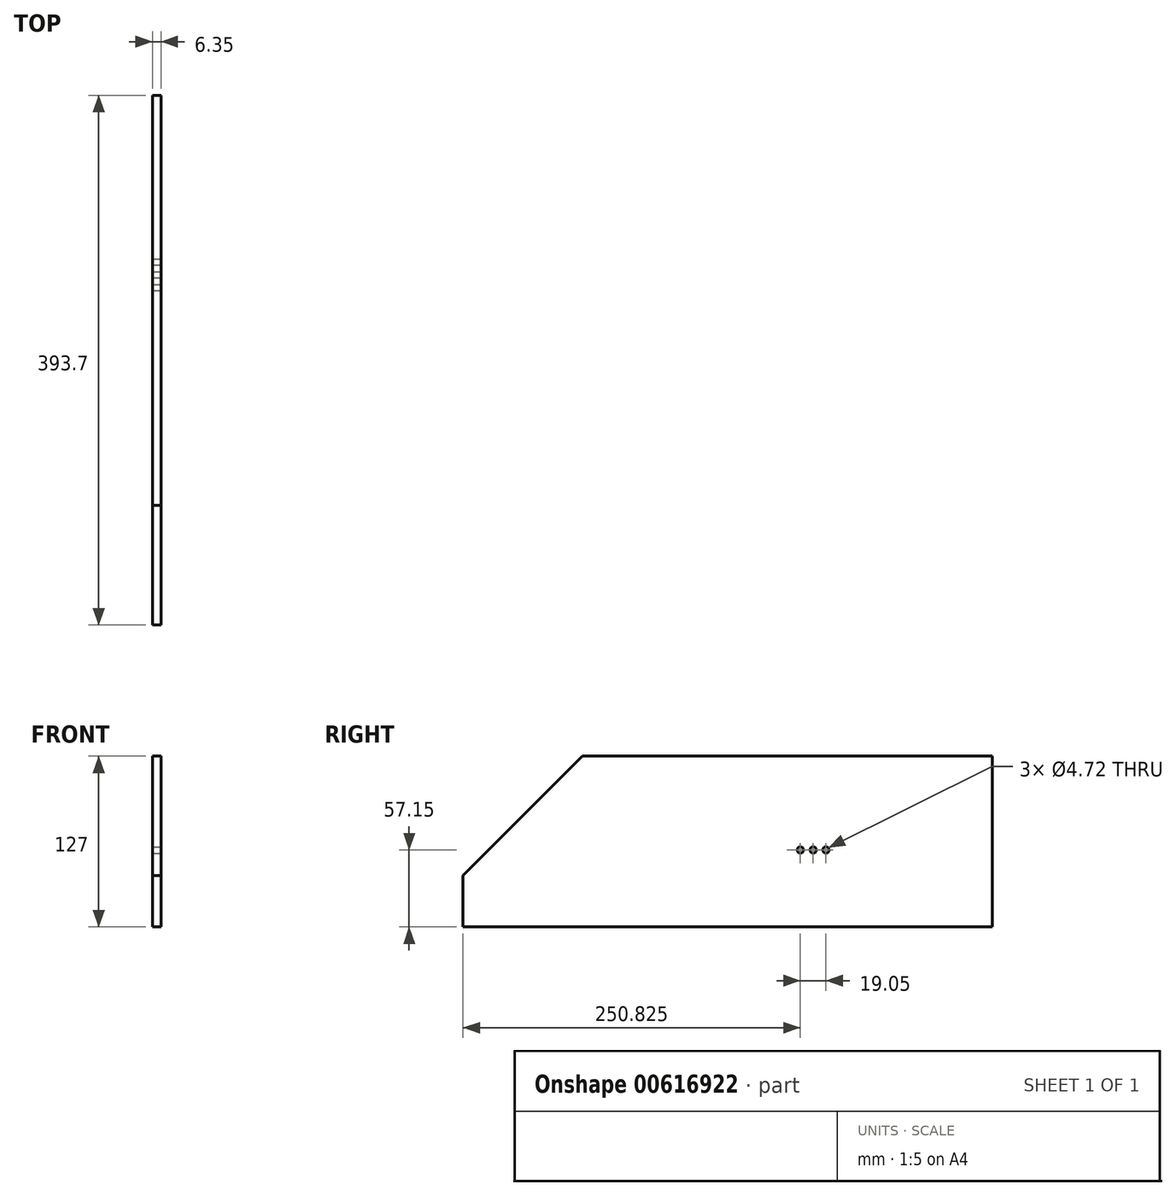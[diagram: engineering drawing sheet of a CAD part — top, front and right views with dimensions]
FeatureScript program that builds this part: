
annotation { "Feature Type Name" : "Feature", "Feature Type Description" : "" }
export const myFeature = defineFeature(function(context is Context, id is Id, definition is map)
    precondition{}
    {
        {
            var Q0;
            Q0=qCreatedBy(makeId("Right.planeOp"),FACE);
            var sketch = newSketch(context, id + "F0", { "sketchPlane" : qUnion([Q0])});
            skLineSegment(sketch, "E0", {"start": v(-196.85, 0) * mm, "end": v(196.85, 0) * mm});
            skLineSegment(sketch, "E1", {"start": v(196.85, 0) * mm, "end": v(196.85, 127) * mm});
            skLineSegment(sketch, "E2", {"start": v(196.85, 127) * mm, "end": v(-107.95, 127) * mm});
            skLineSegment(sketch, "E3", {"start": v(-107.95, 127) * mm, "end": v(-196.85, 38.1) * mm});
            skLineSegment(sketch, "E4", {"start": v(-196.85, 38.1) * mm, "end": v(-196.85, 0) * mm});
            skLineSegment(sketch, "E5", {"start": v(-107.95, 127) * mm, "end": v(-107.95, 0) * mm, "construction": true});
            skSolve(sketch);
        }
        {
            var Q0;
            Q0=qSketchRegion(id+"F0",true);
            extrude(context, id + "F1", {"entities" : qUnion([Q0]), "depth" : 6.35 * mm, "offsetDistance" : 25.4 * mm});
        }
        {
            var Q0;
            Q0=makeQuery(id+"F1.opExtrude","CAP_FACE",FACE,{"disambiguationData":[OSD([sQuery(id+"F0.wireOp",EDGE,"E0"),sQuery(id+"F0.wireOp",EDGE,"E1"),sQuery(id+"F0.wireOp",EDGE,"E2"),sQuery(id+"F0.wireOp",EDGE,"E3"),sQuery(id+"F0.wireOp",EDGE,"E4")])],"isStart":false});
            var sketch = newSketch(context, id + "F2", { "sketchPlane" : qUnion([Q0])});
            skCircle(sketch, "E6", {"center": v(53.98, 57.15) * mm, "radius": 2.36 * mm});
            skCircle(sketch, "E7", {"center": v(63.5, 57.15) * mm, "radius": 2.36 * mm});
            skCircle(sketch, "E8", {"center": v(73.02, 57.15) * mm, "radius": 2.36 * mm});
            skLineSegment(sketch, "E9", {"start": v(63.5, 57.15) * mm, "end": v(63.5, 0) * mm, "construction": true});
            skSolve(sketch);
        }
        {
            var Q0;
            Q0=makeQuery(id+"F2.imprint","IMPRINT",FACE,{"disambiguationData":[TD([[makeQuery(id+"F2.imprint","IMPRINT",EDGE,{"derivedFrom":sQuery(id+"F2.wireOp",EDGE,"E6")}),1.0]])]});
            var Q1;
            Q1=makeQuery(id+"F2.imprint","IMPRINT",FACE,{"disambiguationData":[TD([[makeQuery(id+"F2.imprint","IMPRINT",EDGE,{"derivedFrom":sQuery(id+"F2.wireOp",EDGE,"E7")}),1.0]])]});
            var Q2;
            Q2=makeQuery(id+"F2.imprint","IMPRINT",FACE,{"disambiguationData":[TD([[makeQuery(id+"F2.imprint","IMPRINT",EDGE,{"derivedFrom":sQuery(id+"F2.wireOp",EDGE,"E8")}),1.0]])]});
            extrude(context, id + "F3", {"entities" : qUnion([Q0, Q1, Q2]), "operationType" : NewBodyOperationType.REMOVE, "endBound" : BoundingType.THROUGH_ALL, "oppositeDirection" : true, "depth" : 25.4 * mm, "offsetDistance" : 25.4 * mm});
        }
    });
